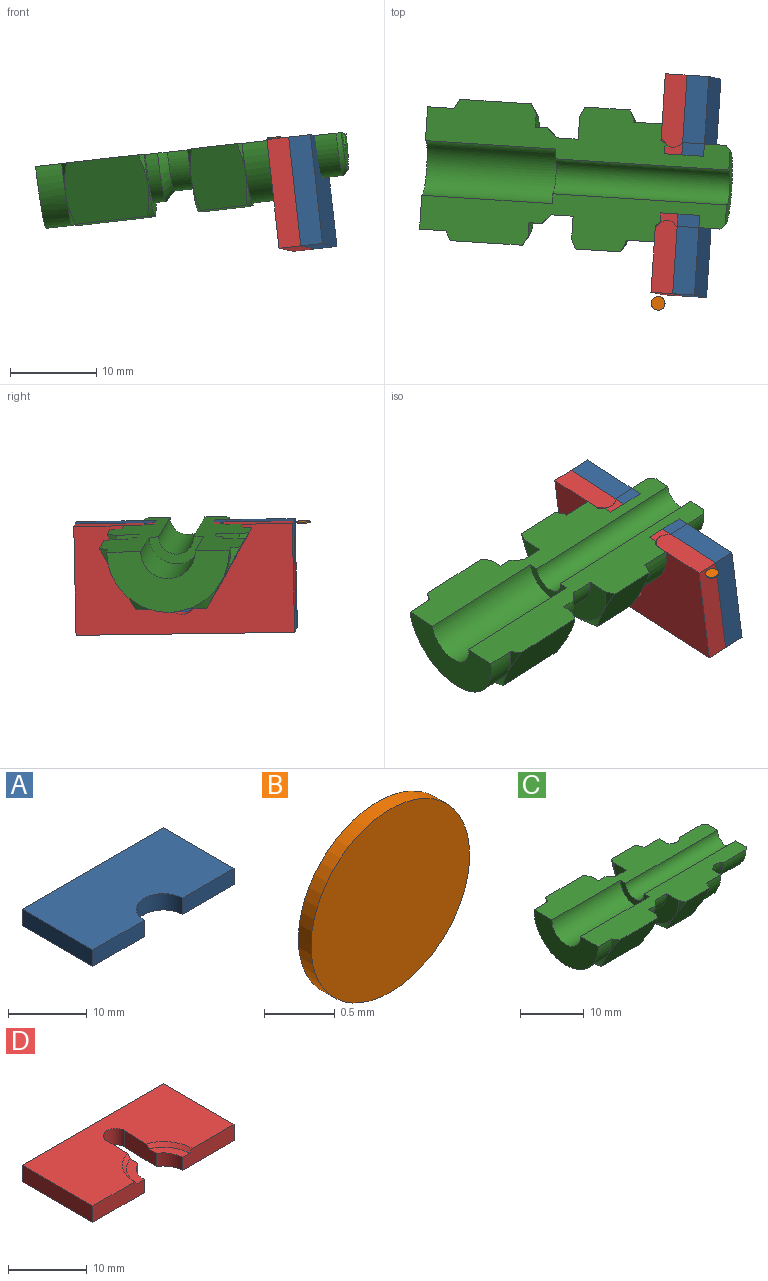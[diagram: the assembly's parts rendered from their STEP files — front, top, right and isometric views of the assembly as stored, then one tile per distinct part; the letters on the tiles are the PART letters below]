
ASSEMBLY  parts=4 mates=7
PART A: 8 faces, bbox 25.4x12.7x2.5 mm
  f0: plane 12.7x2.54mm, normal (-1,0,0), area 32.3mm2, adj f3,f4,f5,f6
  f1: cylinder r=3.43mm len=6.87mm, axis (0,0,1), area 27.4mm2, adj f3,f4,f6,f7
  f2: plane 12.7x2.54mm, normal (1,0,0), area 32.3mm2, adj f3,f4,f5,f7
  f3: plane 25.4x12.7mm, normal (0,0,-1), area 304.1mm2, adj f0,f1,f2,f5,f6,f7
  f4: plane 25.4x12.7mm, normal (0,0,1), area 304.1mm2, adj f0,f1,f2,f5,f6,f7
  f5: plane 25.4x2.54mm, normal (0,1,0), area 64.5mm2, adj f0,f2,f3,f4
  f6: plane 9.27x2.54mm, normal (0,-1,0), area 23.5mm2, adj f0,f1,f3,f4
  f7: plane 9.27x2.54mm, normal (0,-1,0), area 23.5mm2, adj f1,f2,f3,f4
PART B: 3 faces, bbox 1.6x0.1x1.6 mm
  f0: cylinder r=0.79mm len=1.59mm, axis (0,1,0), area 0.6mm2, adj f1,f2
  f1: plane 1.59x1.59mm, normal (0,-1,0), area 2mm2, adj f0
  f2: plane 1.59x1.59mm, normal (0,1,0), area 2mm2, adj f0
PART C: 44 faces, bbox 36.2x17.2x8.9 mm
  f0: plane 10.31x7.77mm, normal (0,-0.87,-0.5), area 75.7mm2, adj f1,f4,f5,f7,f8,f43
  f1: plane 10.31x8.87mm, normal (0,0,-1), area 75.7mm2, adj f0,f2,f3,f4,f8,f9
  f2: plane 10.31x7.77mm, normal (0,0.87,-0.5), area 75.7mm2, adj f1,f3,f6,f9,f10,f42
  f3: cone r=7.11mm half-angle=60deg, axis (1,0,0), area 4.3mm2, adj f1,f2,f11
  f4: cone r=7.11mm half-angle=60deg, axis (1,0,0), area 5mm2, adj f0,f1,f11
  f5: cone r=7.11mm half-angle=60deg, axis (1,0,0), area 2.5mm2, adj f0,f11,f43
  f6: cone r=7.11mm half-angle=60deg, axis (1,0,0), area 2.5mm2, adj f2,f11,f42
  f7: cone r=7.11mm half-angle=60deg, axis (-1,0,0), area 2.5mm2, adj f0,f12,f43
  f8: cone r=7.11mm half-angle=60deg, axis (-1,0,0), area 4.3mm2, adj f0,f1,f12
  f9: cone r=7.11mm half-angle=60deg, axis (-1,0,0), area 5mm2, adj f1,f2,f12
  f10: cone r=7.11mm half-angle=60deg, axis (-1,0,0), area 2.5mm2, adj f2,f12,f42
  f11: cylinder r=7.11mm len=14.22mm, axis (-1,0,0), area 68.1mm2, adj f3,f4,f5,f6,f13,f42,f43
  f12: plane 14.39x7.3mm, normal (1,0,0), area 31mm2, adj f7,f8,f9,f10,f14,f42,f43
  f13: plane 14.31x7.2mm, normal (-1,0,0), area 63.6mm2, adj f11,f15,f42,f43
  f14: cylinder r=5.56mm len=11.11mm, axis (-1,0,0), area 25.5mm2, adj f12,f16,f42,f43
  f15: cylinder r=3.17mm len=15.24mm, axis (1,0,0), area 152mm2, adj f13,f17,f42,f43
  f16: cone r=4.48mm half-angle=45deg, axis (-1,0,0), area 24.1mm2, adj f14,f18,f42,f43
  f17: plane 6.41x3.23mm, normal (-1,0,0), area 9.4mm2, adj f15,f19,f42,f43
  f18: cylinder r=4.48mm len=8.95mm, axis (-1,0,0), area 35.7mm2, adj f16,f20,f42,f43
  f19: cylinder r=2.03mm len=20.32mm, axis (1,0,0), area 129.7mm2, adj f17,f21,f42,f43
  f20: plane 14.51x7.36mm, normal (-1,0,0), area 48.7mm2, adj f18,f22,f23,f24,f25,f42,f43
  f21: plane 8.69x4.41mm, normal (1,0,0), area 22.3mm2, adj f19,f26,f42,f43
  f22: cone r=8.25mm half-angle=65deg, axis (1,0,0), area 2.4mm2, adj f20,f27,f42
  f23: cone r=8.25mm half-angle=65deg, axis (1,0,0), area 2.4mm2, adj f20,f28,f43
  f24: cone r=8.25mm half-angle=65deg, axis (1,0,0), area 4.1mm2, adj f20,f28,f29
  f25: cone r=8.25mm half-angle=65deg, axis (1,0,0), area 4.8mm2, adj f20,f27,f29
  f26: cone r=4.86mm half-angle=45deg, axis (-1,0,0), area 11.8mm2, adj f21,f30,f42,f43
  f27: plane 7.78x6.99mm, normal (0,0.87,-0.5), area 49.5mm2, adj f22,f25,f29,f31,f32,f42
  f28: plane 7.78x6.99mm, normal (0,-0.87,-0.5), area 49.5mm2, adj f23,f24,f29,f33,f34,f43
  f29: plane 8.89x6.99mm, normal (0,0,-1), area 49.5mm2, adj f24,f25,f27,f28,f31,f34
  f30: cylinder r=4.86mm len=9.73mm, axis (1,0,0), area 77mm2, adj f26,f35,f42,f43
  f31: cone r=8.25mm half-angle=65deg, axis (-1,0,0), area 4.8mm2, adj f27,f29,f36
  f32: cone r=8.25mm half-angle=65deg, axis (-1,0,0), area 1.7mm2, adj f27,f36,f42
  f33: cone r=8.25mm half-angle=65deg, axis (-1,0,0), area 2.4mm2, adj f28,f36,f43
  f34: cone r=8.25mm half-angle=65deg, axis (-1,0,0), area 4.8mm2, adj f28,f29,f36
  f35: cone r=4.63mm half-angle=45deg, axis (1,0,0), area 5mm2, adj f30,f37,f42,f43
  f36: plane 14.51x7.36mm, normal (1,0,0), area 6.3mm2, adj f31,f32,f33,f34,f38,f42,f43
  f37: torus R=5.52mm, axis (-1,0,0), area 13.7mm2, adj f35,f39,f42,f43
  f38: cylinder r=6.86mm len=13.72mm, axis (-1,0,0), area 71.1mm2, adj f36,f40,f42,f43
  f39: torus R=5.52mm, axis (-1,0,0), area 10.9mm2, adj f37,f41,f42,f43
  f40: plane 13.86x7mm, normal (1,0,0), area 35.3mm2, adj f38,f41,f42,f43
  f41: cone r=4.95mm half-angle=36deg, axis (-1,0,0), area 11.5mm2, adj f39,f40,f42,f43
  f42: plane 35.56x6.22mm, normal (0,0,1), area 148.3mm2, adj f2,f6,f10,f11,f12,f13,f14,f15
  f43: plane 35.56x6.22mm, normal (0,0,1), area 148.3mm2, adj f0,f5,f7,f11,f12,f13,f14,f15
PART D: 16 faces, bbox 25.4x12.7x2.5 mm
  f0: plane 25.4x12.7mm, normal (0,0,1), area 264.2mm2, adj f3,f5,f7,f8,f9,f10,f11,f13
  f1: cylinder r=3.43mm len=3.1mm, axis (0,0,1), area 7.9mm2, adj f2,f4,f5,f14
  f2: plane 25.4x12.7mm, normal (0,0,-1), area 282.5mm2, adj f1,f5,f6,f7,f8,f9,f10,f13
  f3: cone r=5.21mm half-angle=45deg, axis (0,0,1), area 4.6mm2, adj f0,f4,f5,f14
  f4: plane 4.48x3.28mm, normal (0,0,1), area 6.2mm2, adj f1,f3,f5,f14
  f5: plane 9.27x2.54mm, normal (0,-1,0), area 22.8mm2, adj f0,f1,f2,f3,f4,f10
  f6: cylinder r=3.43mm len=2.98mm, axis (0,0,1), area 7.4mm2, adj f2,f7,f12,f15
  f7: plane 9.27x2.54mm, normal (0,-1,0), area 22.8mm2, adj f0,f2,f6,f9,f11,f12
  f8: plane 25.4x2.54mm, normal (0,1,0), area 64.5mm2, adj f0,f2,f9,f10
  f9: plane 12.7x2.54mm, normal (1,0,0), area 32.3mm2, adj f0,f2,f7,f8
  f10: plane 12.7x2.54mm, normal (-1,0,0), area 32.3mm2, adj f0,f2,f5,f8
  f11: cone r=5.21mm half-angle=45deg, axis (0,0,1), area 4.3mm2, adj f0,f7,f12,f15
  f12: plane 4.36x3mm, normal (0,0,1), area 5.8mm2, adj f6,f7,f11,f15
  f13: cylinder r=1.59mm len=3.17mm, axis (0,0,1), area 12.5mm2, adj f0,f2,f14,f15
  f14: plane 5.81x2.55mm, normal (1,-0.04,0), area 13.9mm2, adj f0,f1,f2,f3,f4,f13
  f15: plane 5.91x2.55mm, normal (-1,0.04,0), area 14.2mm2, adj f0,f2,f6,f11,f12,f13
PLACE A rot(axis=(-0.53,0.56,-0.63),119.2deg) t=(32.05,11.61,35.06)mm
PLACE B rot(axis=(0.58,0.55,0.6),113.6deg) t=(24.48,-1.86,34.63)mm
PLACE C rot(axis=(-0.13,-0.86,-0.5),7.5deg) t=(-2.71,13.85,31.15)mm
PLACE D rot(axis=(-0.63,-0.58,0.52),122.2deg) t=(24.49,12.1,34.21)mm
MATE planar D.f5 <-> A.f7  axis (-0.11,0.02,0.99) through (24.91,-0.65,34.53)mm
MATE planar C.f43 <-> D.f5  axis (-0.11,0.02,0.99) through (9.51,7.5,32.64)mm
MATE planar B.f0 <-> D.f5  axis (0.11,-0.02,-0.99) through (24.49,-1.86,34.51)mm
MATE planar A.f3 <-> D.f2  axis (-0.99,0.06,-0.11) through (27.74,11.8,27.89)mm
MATE planar D.f0 <-> C.f40  axis (-0.99,0.06,-0.11) through (25.26,11.94,27.31)mm
MATE cylindrical C.f30 <-> D.f1  axis (0.99,-0.06,0.11) through (29.48,11.78,34.77)mm
MATE cylindrical A.f1 <-> C.f30  axis (0.99,-0.06,0.11) through (29.53,11.78,34.78)mm
